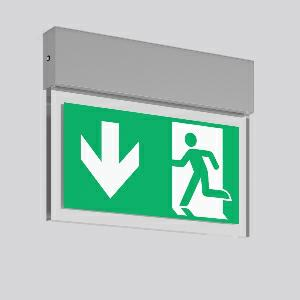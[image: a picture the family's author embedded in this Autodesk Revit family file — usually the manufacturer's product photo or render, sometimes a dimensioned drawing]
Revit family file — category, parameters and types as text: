
# Revit family: halyxx_671737_004_1_89_82a0
name_source: partatom
category: Lighting Fixtures
units: mm (PartAtom-declared; Revit-internal decimal feet)

## family parameters
Cut with Voids When Loaded = No
Host = Face
Light Source = No
Part Type = Normal
Room Calculation Point = No
Round Connector Dimension = Use Diameter
Shared = No

## types (1)
- HALYXX (1 x LED Modul 840, 90 lm, 4000)
    Apparent Load = 4 VA
    Approval mark = CE
    CIE Flux Codes = 18 45 74 52 100
    Color Rendering = 80
    Color Temperature = 4000
    Default Elevation = 1800 mm
    Description = Series: HALYXX
Luminaire for escape route identification. Housing: extruded aluminium profile, anodised or powder-coated. Display panel: highly transparent panel, plastic, with legend on one side/both sides. Driver integrated. Suitable for connection to central battery systems. With AC Control monitoring module for LUXIFAIR central battery units. Please indicate legend number when placing your order! 
Colour: anodised aluminium
Length: 340 mm
Width: 40 mm
Height: 270 mm
Weight: 2.1 kg
Operating mode: maintained power mode
Viewing Distance: 30 m
Lamp: LED
Socket: without socket
Colour temperature: 4000K
Colour rendering index (CRI): 80
System power: 4.1 W
Rated luminous flux: 90 lm
Luminous flux, emergency: 90
System power, emergency: 3.9 W
Control gear: Regulated power supply
Protection class: I
Type of protection: IP 40
    Height = 270 mm
    Lamp = 1 x LED Modul 840
    Lamp Light Flux = 90 lm
    Lamp count = 1
    Length = 340 mm
    Lifetime = 50000 h
    Luminous efficacy = 22 lm/W
    Manufacturer = RZB
    ModVariant = No
    Model = 671737.004.1.89
    Mounting Place = Ceiling
    Mounting Type = Surface mounted
    Number of Poles = 1
    OnlyDefault = Yes
    Power Factor = 1
    Product Name = HALYXX
    Product group = Surface mounted ceiling luminaires
    ProductGroupID = 303
    Protection Class = Protection class I
    Protection Degree = IP 40
    RLX_Detail_Level = 1
    RLX_Emergency_Light_Flux = 90 lm
    RLX_Emergency_Type = 3
    RLX_Emergency_Type_DB = Yes
    RlxData = <blob elided: 55001 chars, md5=a160079c>
    Socket = socket
    Standby Power = 0 W
    System Light Flux = 90 lm
    System Power = 4 W
    Type Comments = Product without accessories
    Type Image = 671744.004.jpg
    URL = http://relux.com
    VarID = ---
    Voltage = 230 V
    Voltage Range = 220-240 V
    Weight = 0.00 kg
    Width = 40 mm  [stored 0.131234 ft]

note: [stored X ft] marks values corroborated as IEEE doubles in the binary element streams (Revit-internal decimal feet)

## geometry (parser evidence)
native form markers: Blend x4, Sweep x13
no freeform markers — native parametric forms only
